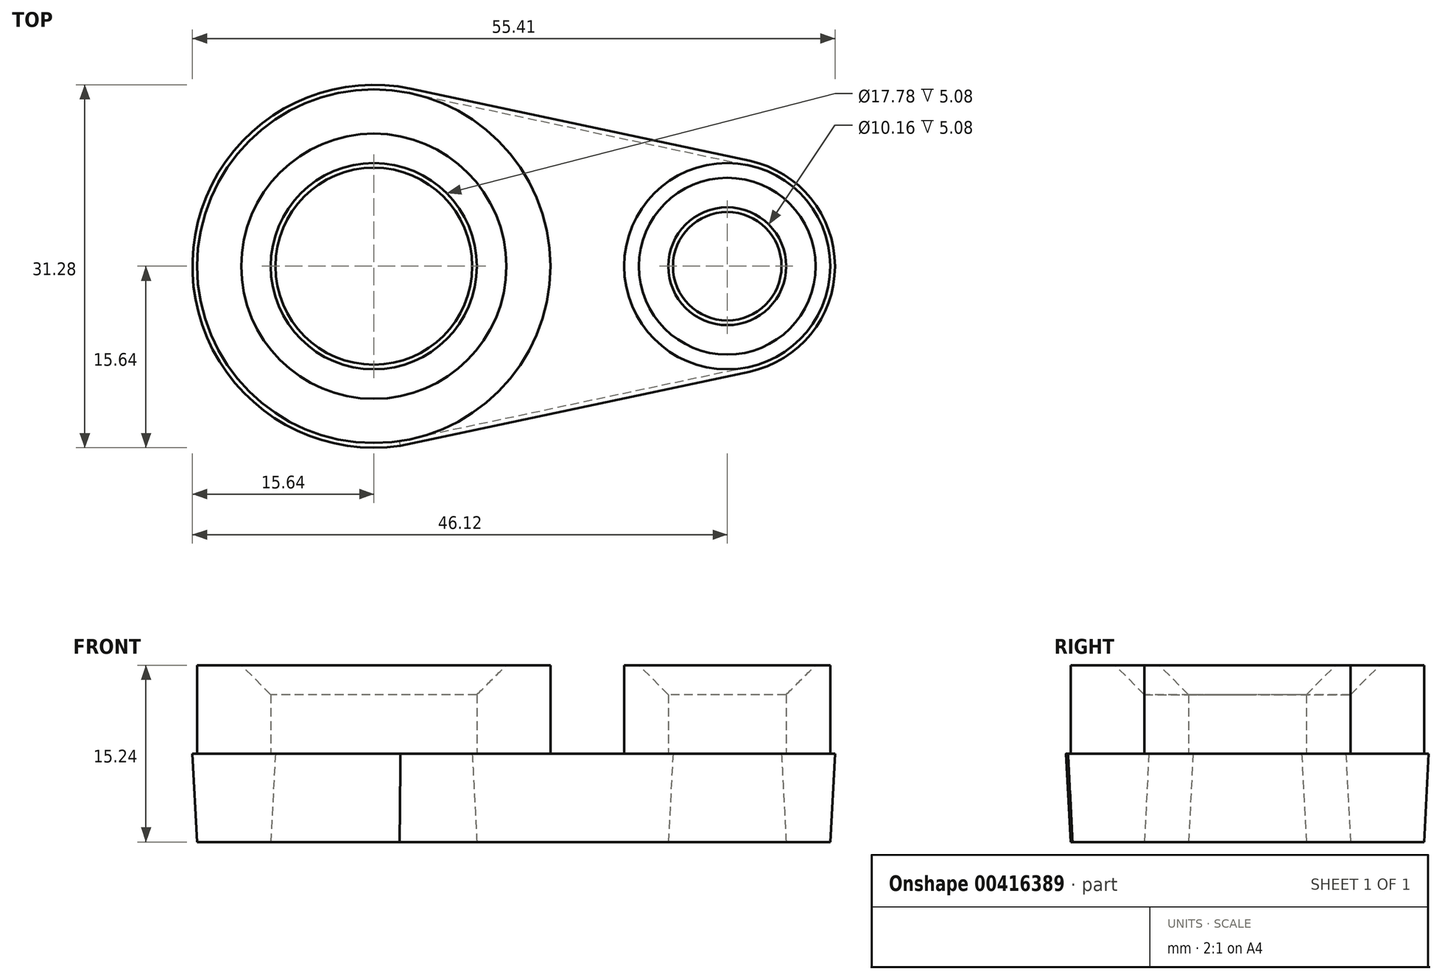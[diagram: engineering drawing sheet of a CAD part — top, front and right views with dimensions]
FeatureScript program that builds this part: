
annotation { "Feature Type Name" : "Feature", "Feature Type Description" : "" }
export const myFeature = defineFeature(function(context is Context, id is Id, definition is map)
    precondition{}
    {
        {
            var Q0;
            Q0=qCreatedBy(makeId("Top.planeOp"),FACE);
            var sketch = newSketch(context, id + "F0", { "sketchPlane" : qUnion([Q0])});
            skCircle(sketch, "E0", {"center": v(0, 0) * mm, "radius": 15.24 * mm});
            skCircle(sketch, "E1", {"center": v(30.48, 0) * mm, "radius": 8.9 * mm});
            skCircle(sketch, "E2", {"center": v(0, 0) * mm, "radius": 8.9 * mm});
            skCircle(sketch, "E3", {"center": v(30.48, 0) * mm, "radius": 5.08 * mm});
            skLineSegment(sketch, "E4", {"start": v(3.17, 14.9) * mm, "end": v(32.33, 8.7) * mm});
            skLineSegment(sketch, "E5", {"start": v(2.23, -15.08) * mm, "end": v(32.32, -8.7) * mm});
            skSolve(sketch);
        }
        {
            var Q0;
            Q0=makeQuery(id+"F0.imprint","IMPRINT",FACE,{"disambiguationData":[TD([[makeQuery(id+"F0.imprint","IMPRINT",EDGE,{"derivedFrom":sQuery(id+"F0.wireOp",EDGE,"E2")}),-1.0]])]});
            var Q1;
            Q1=makeQuery(id+"F0.imprint","IMPRINT",FACE,{"disambiguationData":[TD([[makeQuery(id+"F0.imprint","IMPRINT",EDGE,{"derivedFrom":sQuery(id+"F0.wireOp",EDGE,"E3")}),-1.0]])]});
            var Q2;
            {var subQ0=sQuery(id+"F0.wireOp",EDGE,"E4");Q2=makeQuery(id+"F0.imprint","IMPRINT",FACE,{"disambiguationData":[TD([[makeQuery(id+"F0.imprint","IMPRINT",EDGE,{"derivedFrom":subQ0}),-1.0]])]});}
            extrude(context, id + "F1", {"entities" : qUnion([Q0, Q1, Q2]), "depth" : 7.62 * mm, "hasDraft" : true, "draftAngle" : 3 * degree});
        }
        {
            var Q0;
            Q0=makeQuery(id+"F1.opExtrude","CAP_FACE",FACE,{"disambiguationData":[OSD([sQuery(id+"F0.wireOp",EDGE,"E0"),sQuery(id+"F0.wireOp",EDGE,"E1"),sQuery(id+"F0.wireOp",EDGE,"E2"),sQuery(id+"F0.wireOp",EDGE,"E3"),sQuery(id+"F0.wireOp",EDGE,"E4"),sQuery(id+"F0.wireOp",EDGE,"E5")])],"isStart":false});
            var sketch = newSketch(context, id + "F2", { "sketchPlane" : qUnion([Q0])});
            skCircle(sketch, "E6", {"center": v(0, 0) * mm, "radius": 8.9 * mm});
            skCircle(sketch, "E7", {"center": v(0, 0) * mm, "radius": 15.24 * mm});
            skCircle(sketch, "E8", {"center": v(30.48, 0) * mm, "radius": 5.08 * mm});
            skCircle(sketch, "E9", {"center": v(30.48, 0) * mm, "radius": 8.9 * mm});
            skSolve(sketch);
        }
        {
            var Q0;
            Q0=makeQuery(id+"F2.imprint","IMPRINT",FACE,{"disambiguationData":[TD([[makeQuery(id+"F2.imprint","IMPRINT",EDGE,{"derivedFrom":sQuery(id+"F2.wireOp",EDGE,"E6")}),-1.0]])]});
            var Q1;
            Q1=makeQuery(id+"F2.imprint","IMPRINT",FACE,{"disambiguationData":[TD([[makeQuery(id+"F2.imprint","IMPRINT",EDGE,{"derivedFrom":sQuery(id+"F2.wireOp",EDGE,"E8")}),-1.0]])]});
            extrude(context, id + "F3", {"entities" : qUnion([Q0, Q1]), "operationType" : NewBodyOperationType.ADD, "depth" : 7.62 * mm});
        }
        {
            var Q0;
            Q0=makeQuery(id+"F3.opExtrude","CAP_EDGE",EDGE,{"disambiguationData":[OSD([sQuery(id+"F2.wireOp",EDGE,"E6")])],"isStart":false});
            var Q1;
            Q1=makeQuery(id+"F3.opExtrude","CAP_EDGE",EDGE,{"disambiguationData":[OSD([sQuery(id+"F2.wireOp",EDGE,"E8")])],"isStart":false});
            chamfer(context, id + "F4", {"entities" : qUnion([Q0, Q1]), "width" : 2.54 * mm, "tangentPropagation" : true});
        }
    });
